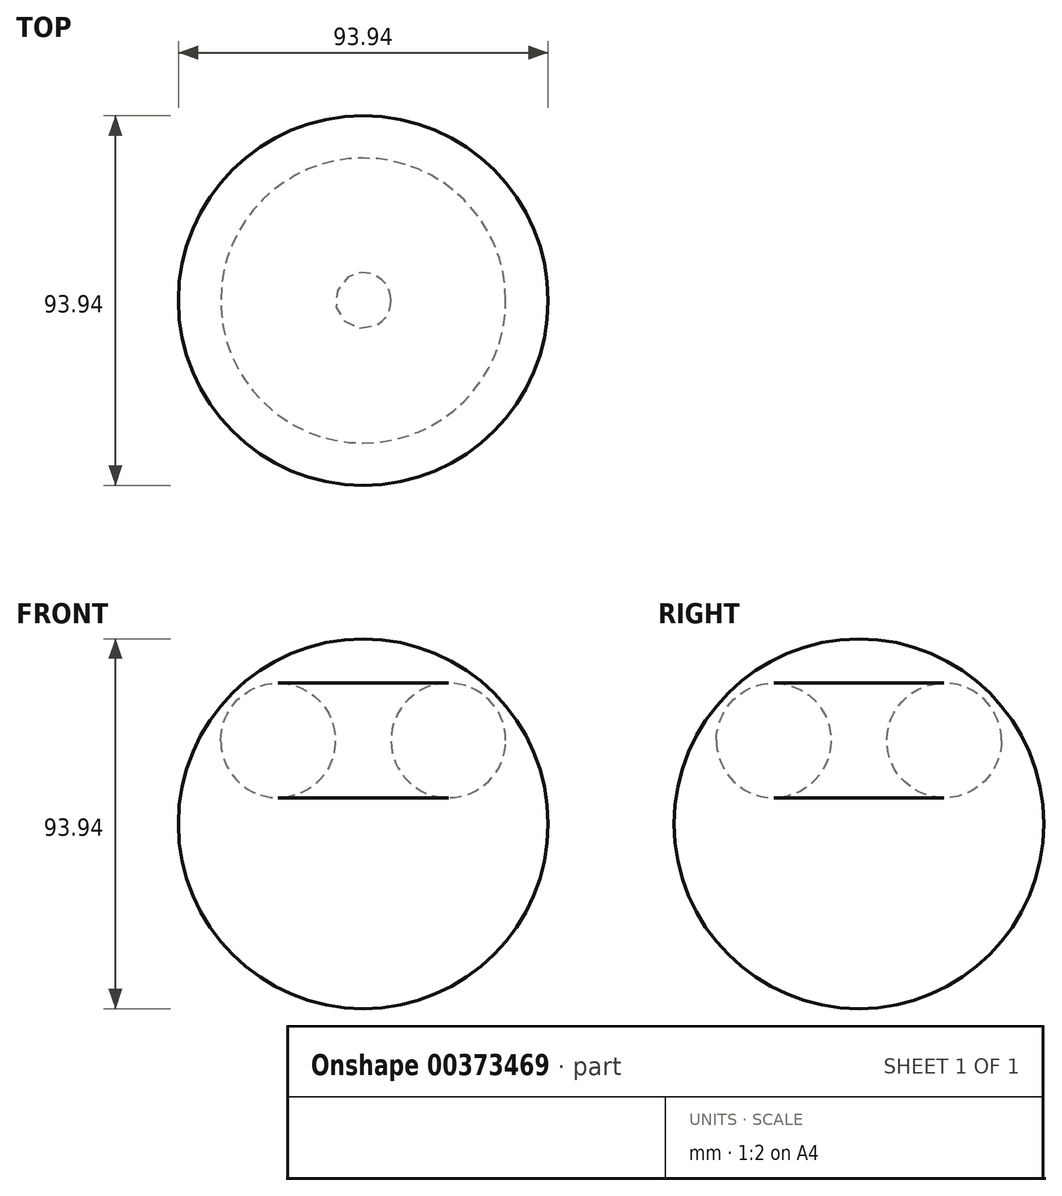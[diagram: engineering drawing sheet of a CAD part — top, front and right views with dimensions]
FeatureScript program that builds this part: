
annotation { "Feature Type Name" : "Feature", "Feature Type Description" : "" }
export const myFeature = defineFeature(function(context is Context, id is Id, definition is map)
    precondition{}
    {
        {
            var Q0;
            Q0=qCreatedBy(makeId("Front.planeOp"),FACE);
            var sketch = newSketch(context, id + "F0", { "sketchPlane" : qUnion([Q0])});
            skCircle(sketch, "E0", {"center": v(0, 0) * mm, "radius": 46.97 * mm});
            skCircle(sketch, "E1", {"center": v(21.64, 21.18) * mm, "radius": 14.56 * mm});
            skLineSegment(sketch, "E2", {"start": v(0, 46.97) * mm, "end": v(0, -46.97) * mm});
            skLineSegment(sketch, "E3", {"start": v(-46.97, 0) * mm, "end": v(46.97, 0) * mm});
            skSolve(sketch);
        }
        {
            var Q0;
            {var subQ0=sQuery(id+"F0.wireOp",EDGE,"E2");var subQ1=sQuery(id+"F0.wireOp",EDGE,"E0");var subQ2=makeQuery(id+"F0.imprint","INTERSECT",VERTEX,{"disambiguationData":[OD(0.0)],"derivedFrom":[subQ1,subQ0]});Q0=makeQuery(id+"F0.imprint","IMPRINT",FACE,{"disambiguationData":[TD([[makeQuery(id+"F0.imprint","IMPRINT",EDGE,{"disambiguationData":[TD([[subQ2,-1.0]])],"derivedFrom":subQ1}),1.0]])]});}
            var Q1;
            {var subQ0=sQuery(id+"F0.wireOp",EDGE,"E2");var subQ1=sQuery(id+"F0.wireOp",EDGE,"E0");var subQ2=makeQuery(id+"F0.imprint","INTERSECT",VERTEX,{"disambiguationData":[OD(1.0)],"derivedFrom":[subQ1,subQ0]});Q1=makeQuery(id+"F0.imprint","IMPRINT",FACE,{"disambiguationData":[TD([[makeQuery(id+"F0.imprint","IMPRINT",EDGE,{"disambiguationData":[TD([[subQ2,1.0]])],"derivedFrom":subQ1}),1.0]])]});}
            var Q2;
            Q2=sQuery(id+"F0.wireOp",EDGE,"E2");
            revolve(context, id + "F1", {"entities" : qUnion([Q0, Q1]), "axis" : qUnion([Q2]), "revolveType" : RevolveType.FULL});
        }
        {
            var Q0;
            Q0=qCreatedBy(makeId("Front.planeOp"),FACE);
            cPlane(context, id + "F2", {"entities" : qUnion([Q0]), "cplaneType" : CPlaneType.OFFSET, "offset" : 47.24 * mm, "width" : 152.4 * mm, "height" : 152.4 * mm});
        }
    });
